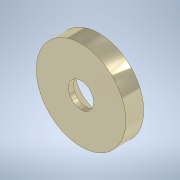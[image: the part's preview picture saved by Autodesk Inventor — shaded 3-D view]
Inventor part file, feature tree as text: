
AUTODESK INVENTOR PART (.ipt)
format: ipt  version: 2022 (Build 260153000, 153)  size: 105,984 bytes
history: native  units: mm
features: sketch x1, extrude x1, hole x1
ambient origin geometry x8: Origin, YZ Plane, XZ Plane, XY Plane, X Axis, Y Axis, Z Axis, Center Point
bodies: Solid1 (feature_tree)
feature tree (3):
  sketch  "Sketch1"  dims[d0=15.875mm d1=3.175mm d2=0.0mm d3=4.496mm d4=8.60806mm d5=8.433mm d6=2.0mm d7=14.3117mm d8=15.664mm d9=0.0mm]
  extrude  "Extrusion1"  Depth=3.175mm TaperAngle=0.0deg
  hole  "Hole1"  [1 undecoded]
note: 1 required parameter value undecoded (feature->parameter linkage not recoverable at this tier; creation-order binding heuristic only, values carry confidence <= 0.55)
